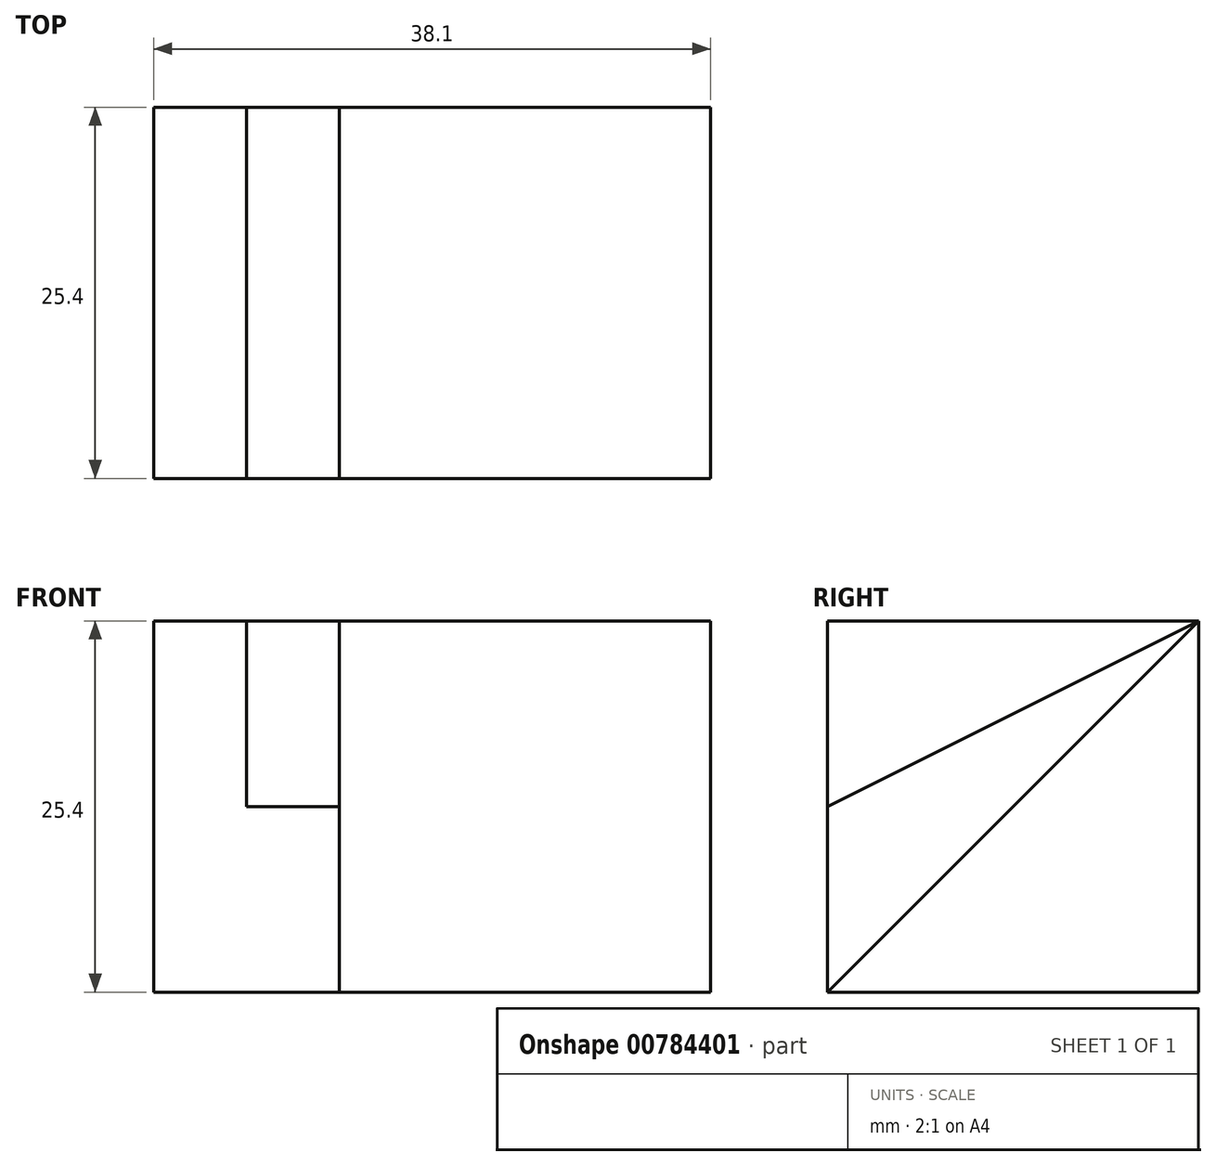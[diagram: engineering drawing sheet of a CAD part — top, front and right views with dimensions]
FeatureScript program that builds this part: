
annotation { "Feature Type Name" : "Feature", "Feature Type Description" : "" }
export const myFeature = defineFeature(function(context is Context, id is Id, definition is map)
    precondition{}
    {
        {
            var Q0;
            Q0=qCreatedBy(makeId("Front.planeOp"),FACE);
            var sketch = newSketch(context, id + "F0", { "sketchPlane" : qUnion([Q0])});
            skLineSegment(sketch, "E0", {"start": v(0, 0) * mm, "end": v(38.1, 0) * mm});
            skLineSegment(sketch, "E1", {"start": v(0, 0) * mm, "end": v(0, 25.4) * mm});
            skLineSegment(sketch, "E2", {"start": v(38.1, 0) * mm, "end": v(38.1, 25.4) * mm});
            skLineSegment(sketch, "E3", {"start": v(38.1, 25.4) * mm, "end": v(0, 25.4) * mm});
            skSolve(sketch);
        }
        {
            var Q0;
            Q0 = qSketchRegion(id + "F0", true);
            extrude(context, id + "F1", {"entities" : qUnion([Q0]), "depth" : 25.4 * mm, "offsetDistance" : 25.4 * mm});
        }
        {
            var Q0;
            Q0=makeQuery(id+"F1.opExtrude","SWEPT_FACE",FACE,{"disambiguationData":[OSD([sQuery(id+"F0.wireOp",EDGE,"E2")])]});
            var sketch = newSketch(context, id + "F2", { "sketchPlane" : qUnion([Q0])});
            skLineSegment(sketch, "E4", {"start": v(0, 0) * mm, "end": v(0, 25.4) * mm});
            skLineSegment(sketch, "E5", {"start": v(0, 25.4) * mm, "end": v(-25.4, 0) * mm});
            skLineSegment(sketch, "E6", {"start": v(-25.4, 0) * mm, "end": v(-25.4, 25.4) * mm});
            skLineSegment(sketch, "E7", {"start": v(-25.4, 25.4) * mm, "end": v(0, 25.4) * mm});
            skSolve(sketch);
        }
        {
            var Q0;
            Q0=makeQuery(id+"F2.imprint","IMPRINT",FACE,{"disambiguationData":[TD([[makeQuery(id+"F2.imprint","IMPRINT",EDGE,{"derivedFrom":sQuery(id+"F2.wireOp",EDGE,"E5")}),-1.0]])]});
            extrude(context, id + "F3", {"entities" : qUnion([Q0]), "operationType" : NewBodyOperationType.REMOVE, "oppositeDirection" : true, "depth" : 25.4 * mm, "offsetDistance" : 25.4 * mm});
        }
        {
            var Q0;
            Q0=makeQuery(id+"F3.boolean.opBoolean","COPY",FACE,{"derivedFrom":makeQuery(id+"F3.opExtrude","CAP_FACE",FACE,{"disambiguationData":[OSD([sQuery(id+"F2.wireOp",EDGE,"E5"),sQuery(id+"F2.wireOp",EDGE,"E6"),sQuery(id+"F2.wireOp",EDGE,"E7")])],"isStart":false})});
            var sketch = newSketch(context, id + "F4", { "sketchPlane" : qUnion([Q0])});
            skLineSegment(sketch, "E8", {"start": v(0, 25.4) * mm, "end": v(-25.4, 12.7) * mm});
            skSolve(sketch);
        }
        {
            var Q0;
            {var subQ0=sQuery(id+"F4.wireOp",EDGE,"E8");Q0=makeQuery(id+"F4.imprint","IMPRINT",FACE,{"disambiguationData":[TD([[makeQuery(id+"F4.imprint","IMPRINT",EDGE,{"derivedFrom":subQ0}),-1.0]])]});}
            extrude(context, id + "F5", {"entities" : qUnion([Q0]), "operationType" : NewBodyOperationType.REMOVE, "oppositeDirection" : true, "depth" : 6.35 * mm, "offsetDistance" : 25.4 * mm});
        }
    });
